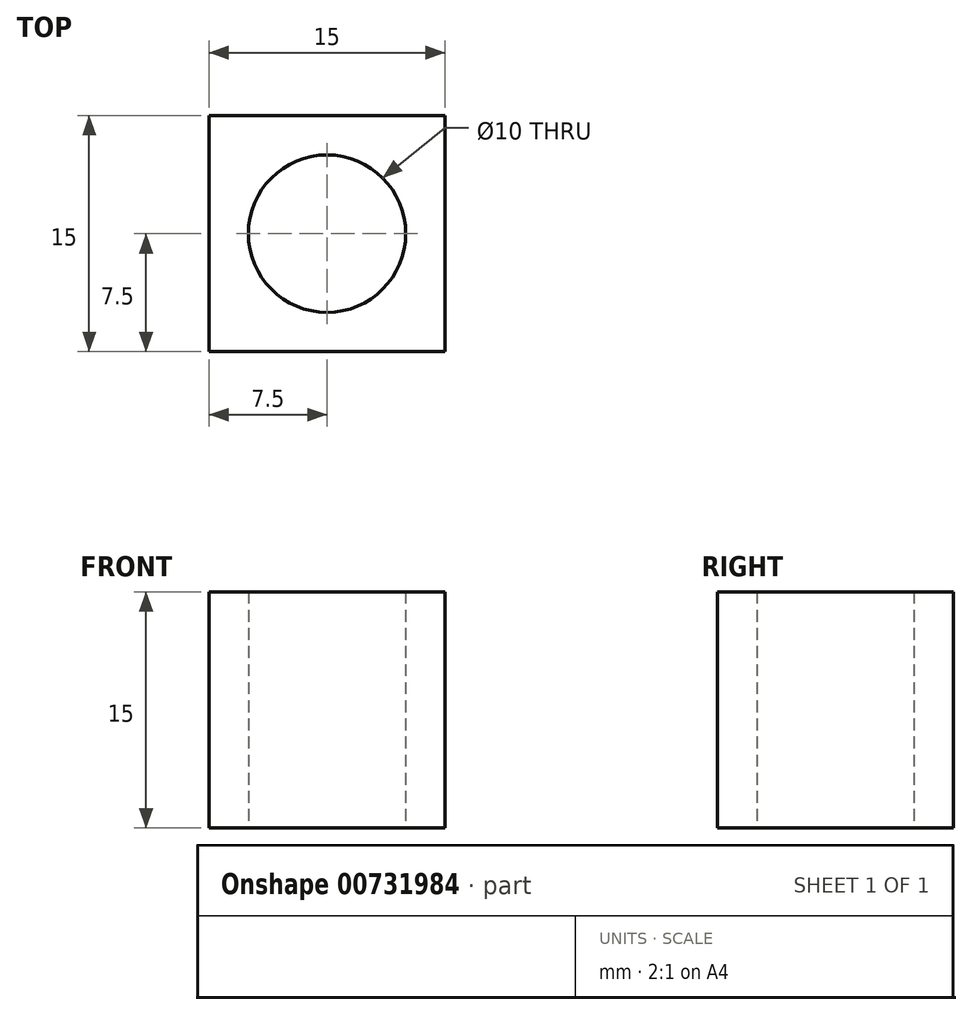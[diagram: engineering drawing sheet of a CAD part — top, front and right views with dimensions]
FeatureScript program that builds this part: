
annotation { "Feature Type Name" : "Feature", "Feature Type Description" : "" }
export const myFeature = defineFeature(function(context is Context, id is Id, definition is map)
    precondition{}
    {
        {
            var Q0;
            Q0=qCreatedBy(makeId("Top.planeOp"),FACE);
            var sketch = newSketch(context, id + "F0", { "sketchPlane" : qUnion([Q0])});
            skLineSegment(sketch, "E0.bottom", {"start": v(0, 15) * mm, "end": v(15, 15) * mm});
            skLineSegment(sketch, "E0.top", {"start": v(0, 0) * mm, "end": v(15, 0) * mm});
            skLineSegment(sketch, "E0.left", {"start": v(0, 15) * mm, "end": v(0, 0) * mm});
            skLineSegment(sketch, "E0.right", {"start": v(15, 15) * mm, "end": v(15, 0) * mm});
            skCircle(sketch, "E1", {"center": v(7.5, 7.5) * mm, "radius": 5 * mm});
            skSolve(sketch);
        }
        {
            var Q0;
            Q0=makeQuery(id+"F0.imprint","IMPRINT",FACE,{"disambiguationData":[TD([[makeQuery(id+"F0.imprint","IMPRINT",EDGE,{"derivedFrom":sQuery(id+"F0.wireOp",EDGE,"E0.bottom")}),-1.0]])]});
            extrude(context, id + "F1", {"entities" : qUnion([Q0]), "depth" : 15 * mm, "offsetDistance" : 25 * mm});
        }
    });
